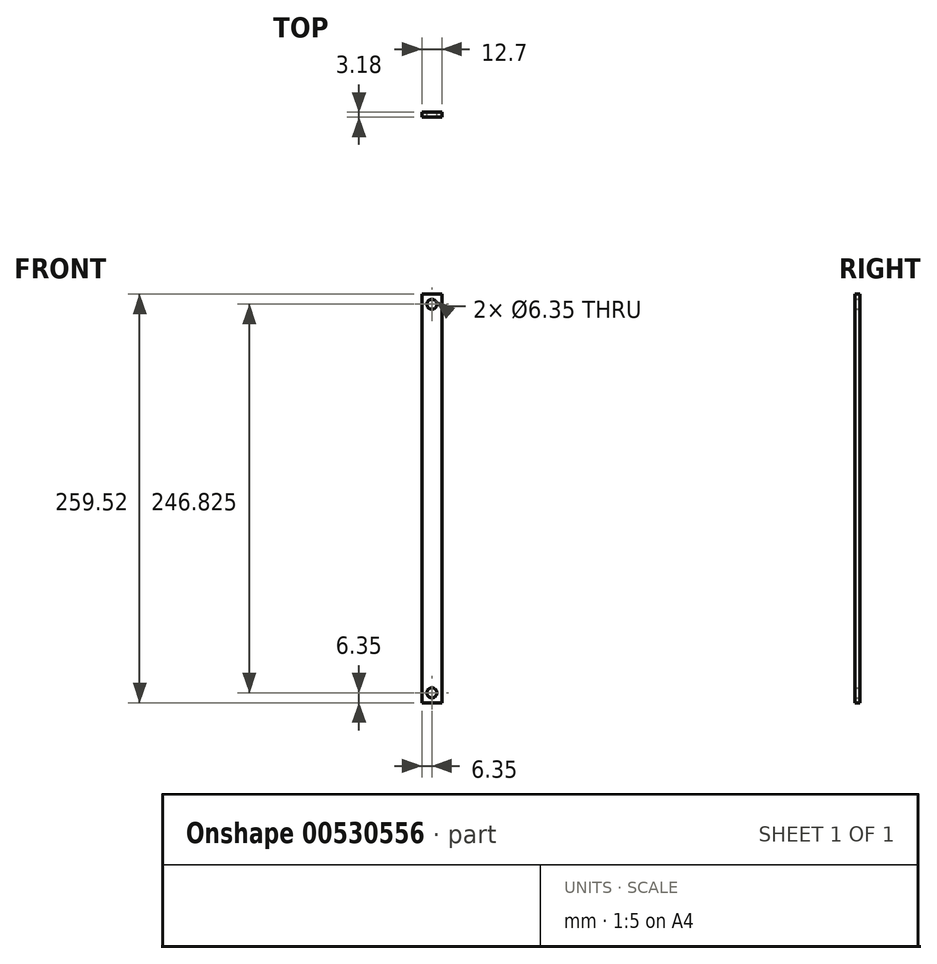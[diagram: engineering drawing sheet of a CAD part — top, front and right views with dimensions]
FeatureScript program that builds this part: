
annotation { "Feature Type Name" : "Feature", "Feature Type Description" : "" }
export const myFeature = defineFeature(function(context is Context, id is Id, definition is map)
    precondition{}
    {
        {
            var Q0;
            Q0=qCreatedBy(makeId("Front.planeOp"),FACE);
            var sketch = newSketch(context, id + "F0", { "sketchPlane" : qUnion([Q0])});
            skLineSegment(sketch, "E0.bottom", {"start": v(0, 0) * mm, "end": v(12.7, 0) * mm});
            skLineSegment(sketch, "E0.top", {"start": v(0, 259.52) * mm, "end": v(12.7, 259.52) * mm});
            skLineSegment(sketch, "E0.left", {"start": v(0, 0) * mm, "end": v(0, 259.52) * mm});
            skLineSegment(sketch, "E0.right", {"start": v(12.7, 0) * mm, "end": v(12.7, 259.52) * mm});
            skCircle(sketch, "E1", {"center": v(6.35, 253.17) * mm, "radius": 3.18 * mm});
            skPoint(sketch, "E1.centerSnap0", {"position": v(6.35, 259.52) * mm});
            skCircle(sketch, "E2", {"center": v(6.35, 6.35) * mm, "radius": 3.18 * mm});
            skPoint(sketch, "E2.centerSnap0", {"position": v(6.35, 0) * mm});
            skSolve(sketch);
        }
        {
            var Q0;
            Q0 = qSketchRegion(id + "F0", true);
            extrude(context, id + "F1", {"entities" : qUnion([Q0]), "depth" : 3.17 * mm, "offsetDistance" : 25.4 * mm});
        }
    });
